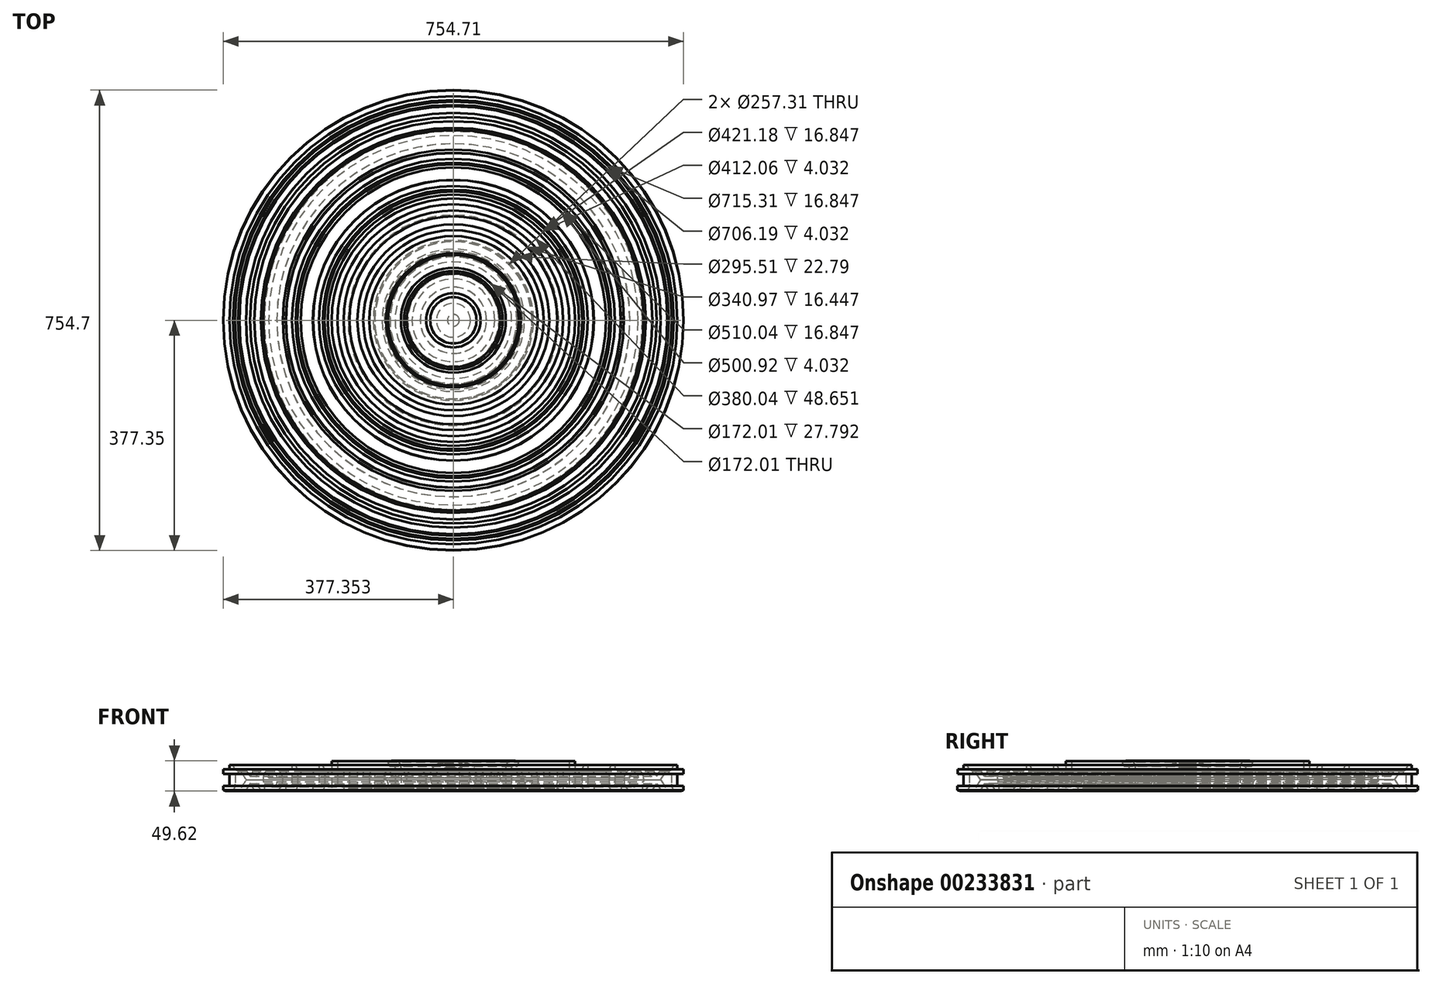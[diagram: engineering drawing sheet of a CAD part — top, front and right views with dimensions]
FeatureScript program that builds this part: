
annotation { "Feature Type Name" : "Feature", "Feature Type Description" : "" }
export const myFeature = defineFeature(function(context is Context, id is Id, definition is map)
    precondition{}
    {
        {
            var Q0;
            Q0=qCreatedBy(makeId("Front.planeOp"),FACE);
            var sketch = newSketch(context, id + "F0", { "sketchPlane" : qUnion([Q0])});
            skText(sketch, "E0", { "text": "Default text", "fontName": "OpenSans-Bold.ttf"});
            const initialGuessF0  = {"E0": [-0.0954, 0.00358, 1, 0, 0.0461]};
            skSetInitialGuess(sketch, initialGuessF0);
            skSolve(sketch);
        }
        {
            var Q0;
            Q0 = qSketchRegion(id + "F0", true);
            extrude(context, id + "F1", {"entities" : qUnion([Q0]), "depth" : 25.4 * mm});
        }
        {
            var Q0;
            Q0=makeQuery(id+"F1.opExtrude","CAP_FACE",FACE,{"disambiguationData":[OSD([sQuery(id+"F0.wireOp",EDGE,"E0.sketch_text.stroke-0"),sQuery(id+"F0.wireOp",EDGE,"E0.sketch_text.stroke-1"),sQuery(id+"F0.wireOp",EDGE,"E0.sketch_text.stroke-2"),sQuery(id+"F0.wireOp",EDGE,"E0.sketch_text.stroke-3"),sQuery(id+"F0.wireOp",EDGE,"E0.sketch_text.stroke-4"),sQuery(id+"F0.wireOp",EDGE,"E0.sketch_text.stroke-5"),sQuery(id+"F0.wireOp",EDGE,"E0.sketch_text.stroke-6"),sQuery(id+"F0.wireOp",EDGE,"E0.sketch_text.stroke-7"),sQuery(id+"F0.wireOp",EDGE,"E0.sketch_text.stroke-8"),sQuery(id+"F0.wireOp",EDGE,"E0.sketch_text.stroke-9"),sQuery(id+"F0.wireOp",EDGE,"E0.sketch_text.stroke-10"),sQuery(id+"F0.wireOp",EDGE,"E0.sketch_text.stroke-11")])],"isStart":true});
            var Q1;
            Q1=makeQuery(id+"F1.opExtrude","CAP_FACE",FACE,{"disambiguationData":[OSD([sQuery(id+"F0.wireOp",EDGE,"E0.sketch_text.stroke-12"),sQuery(id+"F0.wireOp",EDGE,"E0.sketch_text.stroke-13"),sQuery(id+"F0.wireOp",EDGE,"E0.sketch_text.stroke-14"),sQuery(id+"F0.wireOp",EDGE,"E0.sketch_text.stroke-15"),sQuery(id+"F0.wireOp",EDGE,"E0.sketch_text.stroke-16"),sQuery(id+"F0.wireOp",EDGE,"E0.sketch_text.stroke-17"),sQuery(id+"F0.wireOp",EDGE,"E0.sketch_text.stroke-18"),sQuery(id+"F0.wireOp",EDGE,"E0.sketch_text.stroke-19"),sQuery(id+"F0.wireOp",EDGE,"E0.sketch_text.stroke-20"),sQuery(id+"F0.wireOp",EDGE,"E0.sketch_text.stroke-21"),sQuery(id+"F0.wireOp",EDGE,"E0.sketch_text.stroke-22"),sQuery(id+"F0.wireOp",EDGE,"E0.sketch_text.stroke-23"),sQuery(id+"F0.wireOp",EDGE,"E0.sketch_text.stroke-24"),sQuery(id+"F0.wireOp",EDGE,"E0.sketch_text.stroke-25"),sQuery(id+"F0.wireOp",EDGE,"E0.sketch_text.stroke-26"),sQuery(id+"F0.wireOp",EDGE,"E0.sketch_text.stroke-27"),sQuery(id+"F0.wireOp",EDGE,"E0.sketch_text.stroke-28"),sQuery(id+"F0.wireOp",EDGE,"E0.sketch_text.stroke-29"),sQuery(id+"F0.wireOp",EDGE,"E0.sketch_text.stroke-30"),sQuery(id+"F0.wireOp",EDGE,"E0.sketch_text.stroke-31")])],"isStart":true});
            var Q2;
            Q2=makeQuery(id+"F1.opExtrude","CAP_FACE",FACE,{"disambiguationData":[OSD([sQuery(id+"F0.wireOp",EDGE,"E0.sketch_text.stroke-32"),sQuery(id+"F0.wireOp",EDGE,"E0.sketch_text.stroke-33"),sQuery(id+"F0.wireOp",EDGE,"E0.sketch_text.stroke-34"),sQuery(id+"F0.wireOp",EDGE,"E0.sketch_text.stroke-35"),sQuery(id+"F0.wireOp",EDGE,"E0.sketch_text.stroke-36"),sQuery(id+"F0.wireOp",EDGE,"E0.sketch_text.stroke-37"),sQuery(id+"F0.wireOp",EDGE,"E0.sketch_text.stroke-38"),sQuery(id+"F0.wireOp",EDGE,"E0.sketch_text.stroke-39"),sQuery(id+"F0.wireOp",EDGE,"E0.sketch_text.stroke-40"),sQuery(id+"F0.wireOp",EDGE,"E0.sketch_text.stroke-41"),sQuery(id+"F0.wireOp",EDGE,"E0.sketch_text.stroke-42"),sQuery(id+"F0.wireOp",EDGE,"E0.sketch_text.stroke-43"),sQuery(id+"F0.wireOp",EDGE,"E0.sketch_text.stroke-44"),sQuery(id+"F0.wireOp",EDGE,"E0.sketch_text.stroke-45"),sQuery(id+"F0.wireOp",EDGE,"E0.sketch_text.stroke-46"),sQuery(id+"F0.wireOp",EDGE,"E0.sketch_text.stroke-47"),sQuery(id+"F0.wireOp",EDGE,"E0.sketch_text.stroke-48"),sQuery(id+"F0.wireOp",EDGE,"E0.sketch_text.stroke-49")])],"isStart":true});
            var Q3;
            Q3=makeQuery(id+"F1.opExtrude","CAP_FACE",FACE,{"disambiguationData":[OSD([sQuery(id+"F0.wireOp",EDGE,"E0.sketch_text.stroke-50"),sQuery(id+"F0.wireOp",EDGE,"E0.sketch_text.stroke-51"),sQuery(id+"F0.wireOp",EDGE,"E0.sketch_text.stroke-52"),sQuery(id+"F0.wireOp",EDGE,"E0.sketch_text.stroke-53"),sQuery(id+"F0.wireOp",EDGE,"E0.sketch_text.stroke-54"),sQuery(id+"F0.wireOp",EDGE,"E0.sketch_text.stroke-55"),sQuery(id+"F0.wireOp",EDGE,"E0.sketch_text.stroke-56"),sQuery(id+"F0.wireOp",EDGE,"E0.sketch_text.stroke-57"),sQuery(id+"F0.wireOp",EDGE,"E0.sketch_text.stroke-58"),sQuery(id+"F0.wireOp",EDGE,"E0.sketch_text.stroke-59"),sQuery(id+"F0.wireOp",EDGE,"E0.sketch_text.stroke-60"),sQuery(id+"F0.wireOp",EDGE,"E0.sketch_text.stroke-61"),sQuery(id+"F0.wireOp",EDGE,"E0.sketch_text.stroke-62"),sQuery(id+"F0.wireOp",EDGE,"E0.sketch_text.stroke-63"),sQuery(id+"F0.wireOp",EDGE,"E0.sketch_text.stroke-64"),sQuery(id+"F0.wireOp",EDGE,"E0.sketch_text.stroke-65"),sQuery(id+"F0.wireOp",EDGE,"E0.sketch_text.stroke-66"),sQuery(id+"F0.wireOp",EDGE,"E0.sketch_text.stroke-67"),sQuery(id+"F0.wireOp",EDGE,"E0.sketch_text.stroke-68"),sQuery(id+"F0.wireOp",EDGE,"E0.sketch_text.stroke-69"),sQuery(id+"F0.wireOp",EDGE,"E0.sketch_text.stroke-70"),sQuery(id+"F0.wireOp",EDGE,"E0.sketch_text.stroke-71"),sQuery(id+"F0.wireOp",EDGE,"E0.sketch_text.stroke-72"),sQuery(id+"F0.wireOp",EDGE,"E0.sketch_text.stroke-73"),sQuery(id+"F0.wireOp",EDGE,"E0.sketch_text.stroke-74")])],"isStart":true});
            var Q4;
            Q4=makeQuery(id+"F1.opExtrude","CAP_FACE",FACE,{"disambiguationData":[OSD([sQuery(id+"F0.wireOp",EDGE,"E0.sketch_text.stroke-75"),sQuery(id+"F0.wireOp",EDGE,"E0.sketch_text.stroke-76"),sQuery(id+"F0.wireOp",EDGE,"E0.sketch_text.stroke-77"),sQuery(id+"F0.wireOp",EDGE,"E0.sketch_text.stroke-78"),sQuery(id+"F0.wireOp",EDGE,"E0.sketch_text.stroke-79"),sQuery(id+"F0.wireOp",EDGE,"E0.sketch_text.stroke-80"),sQuery(id+"F0.wireOp",EDGE,"E0.sketch_text.stroke-81"),sQuery(id+"F0.wireOp",EDGE,"E0.sketch_text.stroke-82"),sQuery(id+"F0.wireOp",EDGE,"E0.sketch_text.stroke-83"),sQuery(id+"F0.wireOp",EDGE,"E0.sketch_text.stroke-84"),sQuery(id+"F0.wireOp",EDGE,"E0.sketch_text.stroke-85"),sQuery(id+"F0.wireOp",EDGE,"E0.sketch_text.stroke-86"),sQuery(id+"F0.wireOp",EDGE,"E0.sketch_text.stroke-87"),sQuery(id+"F0.wireOp",EDGE,"E0.sketch_text.stroke-88"),sQuery(id+"F0.wireOp",EDGE,"E0.sketch_text.stroke-89"),sQuery(id+"F0.wireOp",EDGE,"E0.sketch_text.stroke-90"),sQuery(id+"F0.wireOp",EDGE,"E0.sketch_text.stroke-91")])],"isStart":true});
            var Q5;
            Q5=makeQuery(id+"F1.opExtrude","CAP_FACE",FACE,{"disambiguationData":[OSD([sQuery(id+"F0.wireOp",EDGE,"E0.sketch_text.stroke-92"),sQuery(id+"F0.wireOp",EDGE,"E0.sketch_text.stroke-93"),sQuery(id+"F0.wireOp",EDGE,"E0.sketch_text.stroke-94"),sQuery(id+"F0.wireOp",EDGE,"E0.sketch_text.stroke-95")])],"isStart":true});
            var Q6;
            Q6=makeQuery(id+"F1.opExtrude","CAP_FACE",FACE,{"disambiguationData":[OSD([sQuery(id+"F0.wireOp",EDGE,"E0.sketch_text.stroke-96"),sQuery(id+"F0.wireOp",EDGE,"E0.sketch_text.stroke-97"),sQuery(id+"F0.wireOp",EDGE,"E0.sketch_text.stroke-98"),sQuery(id+"F0.wireOp",EDGE,"E0.sketch_text.stroke-99"),sQuery(id+"F0.wireOp",EDGE,"E0.sketch_text.stroke-100"),sQuery(id+"F0.wireOp",EDGE,"E0.sketch_text.stroke-101"),sQuery(id+"F0.wireOp",EDGE,"E0.sketch_text.stroke-102"),sQuery(id+"F0.wireOp",EDGE,"E0.sketch_text.stroke-103"),sQuery(id+"F0.wireOp",EDGE,"E0.sketch_text.stroke-104"),sQuery(id+"F0.wireOp",EDGE,"E0.sketch_text.stroke-105"),sQuery(id+"F0.wireOp",EDGE,"E0.sketch_text.stroke-106"),sQuery(id+"F0.wireOp",EDGE,"E0.sketch_text.stroke-107"),sQuery(id+"F0.wireOp",EDGE,"E0.sketch_text.stroke-108"),sQuery(id+"F0.wireOp",EDGE,"E0.sketch_text.stroke-109"),sQuery(id+"F0.wireOp",EDGE,"E0.sketch_text.stroke-110"),sQuery(id+"F0.wireOp",EDGE,"E0.sketch_text.stroke-111"),sQuery(id+"F0.wireOp",EDGE,"E0.sketch_text.stroke-112"),sQuery(id+"F0.wireOp",EDGE,"E0.sketch_text.stroke-113")])],"isStart":true});
            var Q7;
            Q7=makeQuery(id+"F1.opExtrude","CAP_FACE",FACE,{"disambiguationData":[OSD([sQuery(id+"F0.wireOp",EDGE,"E0.sketch_text.stroke-114"),sQuery(id+"F0.wireOp",EDGE,"E0.sketch_text.stroke-115"),sQuery(id+"F0.wireOp",EDGE,"E0.sketch_text.stroke-116"),sQuery(id+"F0.wireOp",EDGE,"E0.sketch_text.stroke-117"),sQuery(id+"F0.wireOp",EDGE,"E0.sketch_text.stroke-118"),sQuery(id+"F0.wireOp",EDGE,"E0.sketch_text.stroke-119"),sQuery(id+"F0.wireOp",EDGE,"E0.sketch_text.stroke-120"),sQuery(id+"F0.wireOp",EDGE,"E0.sketch_text.stroke-121"),sQuery(id+"F0.wireOp",EDGE,"E0.sketch_text.stroke-122"),sQuery(id+"F0.wireOp",EDGE,"E0.sketch_text.stroke-123"),sQuery(id+"F0.wireOp",EDGE,"E0.sketch_text.stroke-124"),sQuery(id+"F0.wireOp",EDGE,"E0.sketch_text.stroke-125"),sQuery(id+"F0.wireOp",EDGE,"E0.sketch_text.stroke-126"),sQuery(id+"F0.wireOp",EDGE,"E0.sketch_text.stroke-127"),sQuery(id+"F0.wireOp",EDGE,"E0.sketch_text.stroke-128"),sQuery(id+"F0.wireOp",EDGE,"E0.sketch_text.stroke-129"),sQuery(id+"F0.wireOp",EDGE,"E0.sketch_text.stroke-130"),sQuery(id+"F0.wireOp",EDGE,"E0.sketch_text.stroke-131")])],"isStart":true});
            var Q8;
            Q8=makeQuery(id+"F1.opExtrude","CAP_FACE",FACE,{"disambiguationData":[OSD([sQuery(id+"F0.wireOp",EDGE,"E0.sketch_text.stroke-132"),sQuery(id+"F0.wireOp",EDGE,"E0.sketch_text.stroke-133"),sQuery(id+"F0.wireOp",EDGE,"E0.sketch_text.stroke-134"),sQuery(id+"F0.wireOp",EDGE,"E0.sketch_text.stroke-135"),sQuery(id+"F0.wireOp",EDGE,"E0.sketch_text.stroke-136"),sQuery(id+"F0.wireOp",EDGE,"E0.sketch_text.stroke-137"),sQuery(id+"F0.wireOp",EDGE,"E0.sketch_text.stroke-138"),sQuery(id+"F0.wireOp",EDGE,"E0.sketch_text.stroke-139"),sQuery(id+"F0.wireOp",EDGE,"E0.sketch_text.stroke-140"),sQuery(id+"F0.wireOp",EDGE,"E0.sketch_text.stroke-141"),sQuery(id+"F0.wireOp",EDGE,"E0.sketch_text.stroke-142"),sQuery(id+"F0.wireOp",EDGE,"E0.sketch_text.stroke-143"),sQuery(id+"F0.wireOp",EDGE,"E0.sketch_text.stroke-144"),sQuery(id+"F0.wireOp",EDGE,"E0.sketch_text.stroke-145"),sQuery(id+"F0.wireOp",EDGE,"E0.sketch_text.stroke-146"),sQuery(id+"F0.wireOp",EDGE,"E0.sketch_text.stroke-147"),sQuery(id+"F0.wireOp",EDGE,"E0.sketch_text.stroke-148"),sQuery(id+"F0.wireOp",EDGE,"E0.sketch_text.stroke-149"),sQuery(id+"F0.wireOp",EDGE,"E0.sketch_text.stroke-150"),sQuery(id+"F0.wireOp",EDGE,"E0.sketch_text.stroke-151")])],"isStart":true});
            var Q9;
            Q9=makeQuery(id+"F1.opExtrude","CAP_FACE",FACE,{"disambiguationData":[OSD([sQuery(id+"F0.wireOp",EDGE,"E0.sketch_text.stroke-152"),sQuery(id+"F0.wireOp",EDGE,"E0.sketch_text.stroke-153"),sQuery(id+"F0.wireOp",EDGE,"E0.sketch_text.stroke-154"),sQuery(id+"F0.wireOp",EDGE,"E0.sketch_text.stroke-155"),sQuery(id+"F0.wireOp",EDGE,"E0.sketch_text.stroke-156"),sQuery(id+"F0.wireOp",EDGE,"E0.sketch_text.stroke-157"),sQuery(id+"F0.wireOp",EDGE,"E0.sketch_text.stroke-158"),sQuery(id+"F0.wireOp",EDGE,"E0.sketch_text.stroke-159"),sQuery(id+"F0.wireOp",EDGE,"E0.sketch_text.stroke-160"),sQuery(id+"F0.wireOp",EDGE,"E0.sketch_text.stroke-161"),sQuery(id+"F0.wireOp",EDGE,"E0.sketch_text.stroke-162"),sQuery(id+"F0.wireOp",EDGE,"E0.sketch_text.stroke-163")])],"isStart":true});
            var Q10;
            Q10=makeQuery(id+"F1.opExtrude","CAP_FACE",FACE,{"disambiguationData":[OSD([sQuery(id+"F0.wireOp",EDGE,"E0.sketch_text.stroke-164"),sQuery(id+"F0.wireOp",EDGE,"E0.sketch_text.stroke-165"),sQuery(id+"F0.wireOp",EDGE,"E0.sketch_text.stroke-166"),sQuery(id+"F0.wireOp",EDGE,"E0.sketch_text.stroke-167"),sQuery(id+"F0.wireOp",EDGE,"E0.sketch_text.stroke-168"),sQuery(id+"F0.wireOp",EDGE,"E0.sketch_text.stroke-169"),sQuery(id+"F0.wireOp",EDGE,"E0.sketch_text.stroke-170"),sQuery(id+"F0.wireOp",EDGE,"E0.sketch_text.stroke-171"),sQuery(id+"F0.wireOp",EDGE,"E0.sketch_text.stroke-172"),sQuery(id+"F0.wireOp",EDGE,"E0.sketch_text.stroke-173"),sQuery(id+"F0.wireOp",EDGE,"E0.sketch_text.stroke-174"),sQuery(id+"F0.wireOp",EDGE,"E0.sketch_text.stroke-175"),sQuery(id+"F0.wireOp",EDGE,"E0.sketch_text.stroke-176"),sQuery(id+"F0.wireOp",EDGE,"E0.sketch_text.stroke-177"),sQuery(id+"F0.wireOp",EDGE,"E0.sketch_text.stroke-178"),sQuery(id+"F0.wireOp",EDGE,"E0.sketch_text.stroke-179"),sQuery(id+"F0.wireOp",EDGE,"E0.sketch_text.stroke-180"),sQuery(id+"F0.wireOp",EDGE,"E0.sketch_text.stroke-181")])],"isStart":true});
            var Q11;
            Q11=makeQuery(id+"F1.opExtrude","CAP_EDGE",EDGE,{"disambiguationData":[OSD([sQuery(id+"F0.wireOp",EDGE,"E0.sketch_text.stroke-3")])],"isStart":true});
            revolve(context, id + "F2", {"entities" : qUnion([Q0, Q1, Q2, Q3, Q4, Q5, Q6, Q7, Q8, Q9, Q10]), "axis" : qUnion([Q11]), "revolveType" : RevolveType.FULL});
        }
        {
            var Q0;
            Q0=makeQuery(id+"F1.opExtrude","SWEPT_BODY",BODY,{"disambiguationData":[OSD([sQuery(id+"F0.wireOp",EDGE,"E0.sketch_text.stroke-164"),sQuery(id+"F0.wireOp",EDGE,"E0.sketch_text.stroke-165"),sQuery(id+"F0.wireOp",EDGE,"E0.sketch_text.stroke-166"),sQuery(id+"F0.wireOp",EDGE,"E0.sketch_text.stroke-167"),sQuery(id+"F0.wireOp",EDGE,"E0.sketch_text.stroke-168"),sQuery(id+"F0.wireOp",EDGE,"E0.sketch_text.stroke-169"),sQuery(id+"F0.wireOp",EDGE,"E0.sketch_text.stroke-170"),sQuery(id+"F0.wireOp",EDGE,"E0.sketch_text.stroke-171"),sQuery(id+"F0.wireOp",EDGE,"E0.sketch_text.stroke-172"),sQuery(id+"F0.wireOp",EDGE,"E0.sketch_text.stroke-173"),sQuery(id+"F0.wireOp",EDGE,"E0.sketch_text.stroke-174"),sQuery(id+"F0.wireOp",EDGE,"E0.sketch_text.stroke-175"),sQuery(id+"F0.wireOp",EDGE,"E0.sketch_text.stroke-176"),sQuery(id+"F0.wireOp",EDGE,"E0.sketch_text.stroke-177"),sQuery(id+"F0.wireOp",EDGE,"E0.sketch_text.stroke-178"),sQuery(id+"F0.wireOp",EDGE,"E0.sketch_text.stroke-179"),sQuery(id+"F0.wireOp",EDGE,"E0.sketch_text.stroke-180"),sQuery(id+"F0.wireOp",EDGE,"E0.sketch_text.stroke-181")])]});
            var Q1;
            Q1=makeQuery(id+"F1.opExtrude","SWEPT_BODY",BODY,{"disambiguationData":[OSD([sQuery(id+"F0.wireOp",EDGE,"E0.sketch_text.stroke-152"),sQuery(id+"F0.wireOp",EDGE,"E0.sketch_text.stroke-153"),sQuery(id+"F0.wireOp",EDGE,"E0.sketch_text.stroke-154"),sQuery(id+"F0.wireOp",EDGE,"E0.sketch_text.stroke-155"),sQuery(id+"F0.wireOp",EDGE,"E0.sketch_text.stroke-156"),sQuery(id+"F0.wireOp",EDGE,"E0.sketch_text.stroke-157"),sQuery(id+"F0.wireOp",EDGE,"E0.sketch_text.stroke-158"),sQuery(id+"F0.wireOp",EDGE,"E0.sketch_text.stroke-159"),sQuery(id+"F0.wireOp",EDGE,"E0.sketch_text.stroke-160"),sQuery(id+"F0.wireOp",EDGE,"E0.sketch_text.stroke-161"),sQuery(id+"F0.wireOp",EDGE,"E0.sketch_text.stroke-162"),sQuery(id+"F0.wireOp",EDGE,"E0.sketch_text.stroke-163")])]});
            var Q2;
            Q2=makeQuery(id+"F1.opExtrude","SWEPT_BODY",BODY,{"disambiguationData":[OSD([sQuery(id+"F0.wireOp",EDGE,"E0.sketch_text.stroke-132"),sQuery(id+"F0.wireOp",EDGE,"E0.sketch_text.stroke-133"),sQuery(id+"F0.wireOp",EDGE,"E0.sketch_text.stroke-134"),sQuery(id+"F0.wireOp",EDGE,"E0.sketch_text.stroke-135"),sQuery(id+"F0.wireOp",EDGE,"E0.sketch_text.stroke-136"),sQuery(id+"F0.wireOp",EDGE,"E0.sketch_text.stroke-137"),sQuery(id+"F0.wireOp",EDGE,"E0.sketch_text.stroke-138"),sQuery(id+"F0.wireOp",EDGE,"E0.sketch_text.stroke-139"),sQuery(id+"F0.wireOp",EDGE,"E0.sketch_text.stroke-140"),sQuery(id+"F0.wireOp",EDGE,"E0.sketch_text.stroke-141"),sQuery(id+"F0.wireOp",EDGE,"E0.sketch_text.stroke-142"),sQuery(id+"F0.wireOp",EDGE,"E0.sketch_text.stroke-143"),sQuery(id+"F0.wireOp",EDGE,"E0.sketch_text.stroke-144"),sQuery(id+"F0.wireOp",EDGE,"E0.sketch_text.stroke-145"),sQuery(id+"F0.wireOp",EDGE,"E0.sketch_text.stroke-146"),sQuery(id+"F0.wireOp",EDGE,"E0.sketch_text.stroke-147"),sQuery(id+"F0.wireOp",EDGE,"E0.sketch_text.stroke-148"),sQuery(id+"F0.wireOp",EDGE,"E0.sketch_text.stroke-149"),sQuery(id+"F0.wireOp",EDGE,"E0.sketch_text.stroke-150"),sQuery(id+"F0.wireOp",EDGE,"E0.sketch_text.stroke-151")])]});
            var Q3;
            Q3=makeQuery(id+"F1.opExtrude","SWEPT_BODY",BODY,{"disambiguationData":[OSD([sQuery(id+"F0.wireOp",EDGE,"E0.sketch_text.stroke-114"),sQuery(id+"F0.wireOp",EDGE,"E0.sketch_text.stroke-115"),sQuery(id+"F0.wireOp",EDGE,"E0.sketch_text.stroke-116"),sQuery(id+"F0.wireOp",EDGE,"E0.sketch_text.stroke-117"),sQuery(id+"F0.wireOp",EDGE,"E0.sketch_text.stroke-118"),sQuery(id+"F0.wireOp",EDGE,"E0.sketch_text.stroke-119"),sQuery(id+"F0.wireOp",EDGE,"E0.sketch_text.stroke-120"),sQuery(id+"F0.wireOp",EDGE,"E0.sketch_text.stroke-121"),sQuery(id+"F0.wireOp",EDGE,"E0.sketch_text.stroke-122"),sQuery(id+"F0.wireOp",EDGE,"E0.sketch_text.stroke-123"),sQuery(id+"F0.wireOp",EDGE,"E0.sketch_text.stroke-124"),sQuery(id+"F0.wireOp",EDGE,"E0.sketch_text.stroke-125"),sQuery(id+"F0.wireOp",EDGE,"E0.sketch_text.stroke-126"),sQuery(id+"F0.wireOp",EDGE,"E0.sketch_text.stroke-127"),sQuery(id+"F0.wireOp",EDGE,"E0.sketch_text.stroke-128"),sQuery(id+"F0.wireOp",EDGE,"E0.sketch_text.stroke-129"),sQuery(id+"F0.wireOp",EDGE,"E0.sketch_text.stroke-130"),sQuery(id+"F0.wireOp",EDGE,"E0.sketch_text.stroke-131")])]});
            var Q4;
            Q4=makeQuery(id+"F1.opExtrude","SWEPT_BODY",BODY,{"disambiguationData":[OSD([sQuery(id+"F0.wireOp",EDGE,"E0.sketch_text.stroke-96"),sQuery(id+"F0.wireOp",EDGE,"E0.sketch_text.stroke-97"),sQuery(id+"F0.wireOp",EDGE,"E0.sketch_text.stroke-98"),sQuery(id+"F0.wireOp",EDGE,"E0.sketch_text.stroke-99"),sQuery(id+"F0.wireOp",EDGE,"E0.sketch_text.stroke-100"),sQuery(id+"F0.wireOp",EDGE,"E0.sketch_text.stroke-101"),sQuery(id+"F0.wireOp",EDGE,"E0.sketch_text.stroke-102"),sQuery(id+"F0.wireOp",EDGE,"E0.sketch_text.stroke-103"),sQuery(id+"F0.wireOp",EDGE,"E0.sketch_text.stroke-104"),sQuery(id+"F0.wireOp",EDGE,"E0.sketch_text.stroke-105"),sQuery(id+"F0.wireOp",EDGE,"E0.sketch_text.stroke-106"),sQuery(id+"F0.wireOp",EDGE,"E0.sketch_text.stroke-107"),sQuery(id+"F0.wireOp",EDGE,"E0.sketch_text.stroke-108"),sQuery(id+"F0.wireOp",EDGE,"E0.sketch_text.stroke-109"),sQuery(id+"F0.wireOp",EDGE,"E0.sketch_text.stroke-110"),sQuery(id+"F0.wireOp",EDGE,"E0.sketch_text.stroke-111"),sQuery(id+"F0.wireOp",EDGE,"E0.sketch_text.stroke-112"),sQuery(id+"F0.wireOp",EDGE,"E0.sketch_text.stroke-113")])]});
            var Q5;
            Q5=makeQuery(id+"F1.opExtrude","SWEPT_BODY",BODY,{"disambiguationData":[OSD([sQuery(id+"F0.wireOp",EDGE,"E0.sketch_text.stroke-92"),sQuery(id+"F0.wireOp",EDGE,"E0.sketch_text.stroke-93"),sQuery(id+"F0.wireOp",EDGE,"E0.sketch_text.stroke-94"),sQuery(id+"F0.wireOp",EDGE,"E0.sketch_text.stroke-95")])]});
            var Q6;
            Q6=makeQuery(id+"F1.opExtrude","SWEPT_BODY",BODY,{"disambiguationData":[OSD([sQuery(id+"F0.wireOp",EDGE,"E0.sketch_text.stroke-75"),sQuery(id+"F0.wireOp",EDGE,"E0.sketch_text.stroke-76"),sQuery(id+"F0.wireOp",EDGE,"E0.sketch_text.stroke-77"),sQuery(id+"F0.wireOp",EDGE,"E0.sketch_text.stroke-78"),sQuery(id+"F0.wireOp",EDGE,"E0.sketch_text.stroke-79"),sQuery(id+"F0.wireOp",EDGE,"E0.sketch_text.stroke-80"),sQuery(id+"F0.wireOp",EDGE,"E0.sketch_text.stroke-81"),sQuery(id+"F0.wireOp",EDGE,"E0.sketch_text.stroke-82"),sQuery(id+"F0.wireOp",EDGE,"E0.sketch_text.stroke-83"),sQuery(id+"F0.wireOp",EDGE,"E0.sketch_text.stroke-84"),sQuery(id+"F0.wireOp",EDGE,"E0.sketch_text.stroke-85"),sQuery(id+"F0.wireOp",EDGE,"E0.sketch_text.stroke-86"),sQuery(id+"F0.wireOp",EDGE,"E0.sketch_text.stroke-87"),sQuery(id+"F0.wireOp",EDGE,"E0.sketch_text.stroke-88"),sQuery(id+"F0.wireOp",EDGE,"E0.sketch_text.stroke-89"),sQuery(id+"F0.wireOp",EDGE,"E0.sketch_text.stroke-90"),sQuery(id+"F0.wireOp",EDGE,"E0.sketch_text.stroke-91")])]});
            var Q7;
            Q7=makeQuery(id+"F1.opExtrude","SWEPT_BODY",BODY,{"disambiguationData":[OSD([sQuery(id+"F0.wireOp",EDGE,"E0.sketch_text.stroke-50"),sQuery(id+"F0.wireOp",EDGE,"E0.sketch_text.stroke-51"),sQuery(id+"F0.wireOp",EDGE,"E0.sketch_text.stroke-52"),sQuery(id+"F0.wireOp",EDGE,"E0.sketch_text.stroke-53"),sQuery(id+"F0.wireOp",EDGE,"E0.sketch_text.stroke-54"),sQuery(id+"F0.wireOp",EDGE,"E0.sketch_text.stroke-55"),sQuery(id+"F0.wireOp",EDGE,"E0.sketch_text.stroke-56"),sQuery(id+"F0.wireOp",EDGE,"E0.sketch_text.stroke-57"),sQuery(id+"F0.wireOp",EDGE,"E0.sketch_text.stroke-58"),sQuery(id+"F0.wireOp",EDGE,"E0.sketch_text.stroke-59"),sQuery(id+"F0.wireOp",EDGE,"E0.sketch_text.stroke-60"),sQuery(id+"F0.wireOp",EDGE,"E0.sketch_text.stroke-61"),sQuery(id+"F0.wireOp",EDGE,"E0.sketch_text.stroke-62"),sQuery(id+"F0.wireOp",EDGE,"E0.sketch_text.stroke-63"),sQuery(id+"F0.wireOp",EDGE,"E0.sketch_text.stroke-64"),sQuery(id+"F0.wireOp",EDGE,"E0.sketch_text.stroke-65"),sQuery(id+"F0.wireOp",EDGE,"E0.sketch_text.stroke-66"),sQuery(id+"F0.wireOp",EDGE,"E0.sketch_text.stroke-67"),sQuery(id+"F0.wireOp",EDGE,"E0.sketch_text.stroke-68"),sQuery(id+"F0.wireOp",EDGE,"E0.sketch_text.stroke-69"),sQuery(id+"F0.wireOp",EDGE,"E0.sketch_text.stroke-70"),sQuery(id+"F0.wireOp",EDGE,"E0.sketch_text.stroke-71"),sQuery(id+"F0.wireOp",EDGE,"E0.sketch_text.stroke-72"),sQuery(id+"F0.wireOp",EDGE,"E0.sketch_text.stroke-73"),sQuery(id+"F0.wireOp",EDGE,"E0.sketch_text.stroke-74")])]});
            var Q8;
            Q8=makeQuery(id+"F1.opExtrude","SWEPT_BODY",BODY,{"disambiguationData":[OSD([sQuery(id+"F0.wireOp",EDGE,"E0.sketch_text.stroke-32"),sQuery(id+"F0.wireOp",EDGE,"E0.sketch_text.stroke-33"),sQuery(id+"F0.wireOp",EDGE,"E0.sketch_text.stroke-34"),sQuery(id+"F0.wireOp",EDGE,"E0.sketch_text.stroke-35"),sQuery(id+"F0.wireOp",EDGE,"E0.sketch_text.stroke-36"),sQuery(id+"F0.wireOp",EDGE,"E0.sketch_text.stroke-37"),sQuery(id+"F0.wireOp",EDGE,"E0.sketch_text.stroke-38"),sQuery(id+"F0.wireOp",EDGE,"E0.sketch_text.stroke-39"),sQuery(id+"F0.wireOp",EDGE,"E0.sketch_text.stroke-40"),sQuery(id+"F0.wireOp",EDGE,"E0.sketch_text.stroke-41"),sQuery(id+"F0.wireOp",EDGE,"E0.sketch_text.stroke-42"),sQuery(id+"F0.wireOp",EDGE,"E0.sketch_text.stroke-43"),sQuery(id+"F0.wireOp",EDGE,"E0.sketch_text.stroke-44"),sQuery(id+"F0.wireOp",EDGE,"E0.sketch_text.stroke-45"),sQuery(id+"F0.wireOp",EDGE,"E0.sketch_text.stroke-46"),sQuery(id+"F0.wireOp",EDGE,"E0.sketch_text.stroke-47"),sQuery(id+"F0.wireOp",EDGE,"E0.sketch_text.stroke-48"),sQuery(id+"F0.wireOp",EDGE,"E0.sketch_text.stroke-49")])]});
            var Q9;
            Q9=makeQuery(id+"F1.opExtrude","SWEPT_BODY",BODY,{"disambiguationData":[OSD([sQuery(id+"F0.wireOp",EDGE,"E0.sketch_text.stroke-12"),sQuery(id+"F0.wireOp",EDGE,"E0.sketch_text.stroke-13"),sQuery(id+"F0.wireOp",EDGE,"E0.sketch_text.stroke-14"),sQuery(id+"F0.wireOp",EDGE,"E0.sketch_text.stroke-15"),sQuery(id+"F0.wireOp",EDGE,"E0.sketch_text.stroke-16"),sQuery(id+"F0.wireOp",EDGE,"E0.sketch_text.stroke-17"),sQuery(id+"F0.wireOp",EDGE,"E0.sketch_text.stroke-18"),sQuery(id+"F0.wireOp",EDGE,"E0.sketch_text.stroke-19"),sQuery(id+"F0.wireOp",EDGE,"E0.sketch_text.stroke-20"),sQuery(id+"F0.wireOp",EDGE,"E0.sketch_text.stroke-21"),sQuery(id+"F0.wireOp",EDGE,"E0.sketch_text.stroke-22"),sQuery(id+"F0.wireOp",EDGE,"E0.sketch_text.stroke-23"),sQuery(id+"F0.wireOp",EDGE,"E0.sketch_text.stroke-24"),sQuery(id+"F0.wireOp",EDGE,"E0.sketch_text.stroke-25"),sQuery(id+"F0.wireOp",EDGE,"E0.sketch_text.stroke-26"),sQuery(id+"F0.wireOp",EDGE,"E0.sketch_text.stroke-27"),sQuery(id+"F0.wireOp",EDGE,"E0.sketch_text.stroke-28"),sQuery(id+"F0.wireOp",EDGE,"E0.sketch_text.stroke-29"),sQuery(id+"F0.wireOp",EDGE,"E0.sketch_text.stroke-30"),sQuery(id+"F0.wireOp",EDGE,"E0.sketch_text.stroke-31")])]});
            var Q10;
            Q10=makeQuery(id+"F1.opExtrude","SWEPT_BODY",BODY,{"disambiguationData":[OSD([sQuery(id+"F0.wireOp",EDGE,"E0.sketch_text.stroke-0"),sQuery(id+"F0.wireOp",EDGE,"E0.sketch_text.stroke-1"),sQuery(id+"F0.wireOp",EDGE,"E0.sketch_text.stroke-2"),sQuery(id+"F0.wireOp",EDGE,"E0.sketch_text.stroke-3"),sQuery(id+"F0.wireOp",EDGE,"E0.sketch_text.stroke-4"),sQuery(id+"F0.wireOp",EDGE,"E0.sketch_text.stroke-5"),sQuery(id+"F0.wireOp",EDGE,"E0.sketch_text.stroke-6"),sQuery(id+"F0.wireOp",EDGE,"E0.sketch_text.stroke-7"),sQuery(id+"F0.wireOp",EDGE,"E0.sketch_text.stroke-8"),sQuery(id+"F0.wireOp",EDGE,"E0.sketch_text.stroke-9"),sQuery(id+"F0.wireOp",EDGE,"E0.sketch_text.stroke-10"),sQuery(id+"F0.wireOp",EDGE,"E0.sketch_text.stroke-11")])]});
            deleteBodies(context, id + "F3", {"entities" : qUnion([Q0, Q1, Q2, Q3, Q4, Q5, Q6, Q7, Q8, Q9, Q10])});
        }
    });
